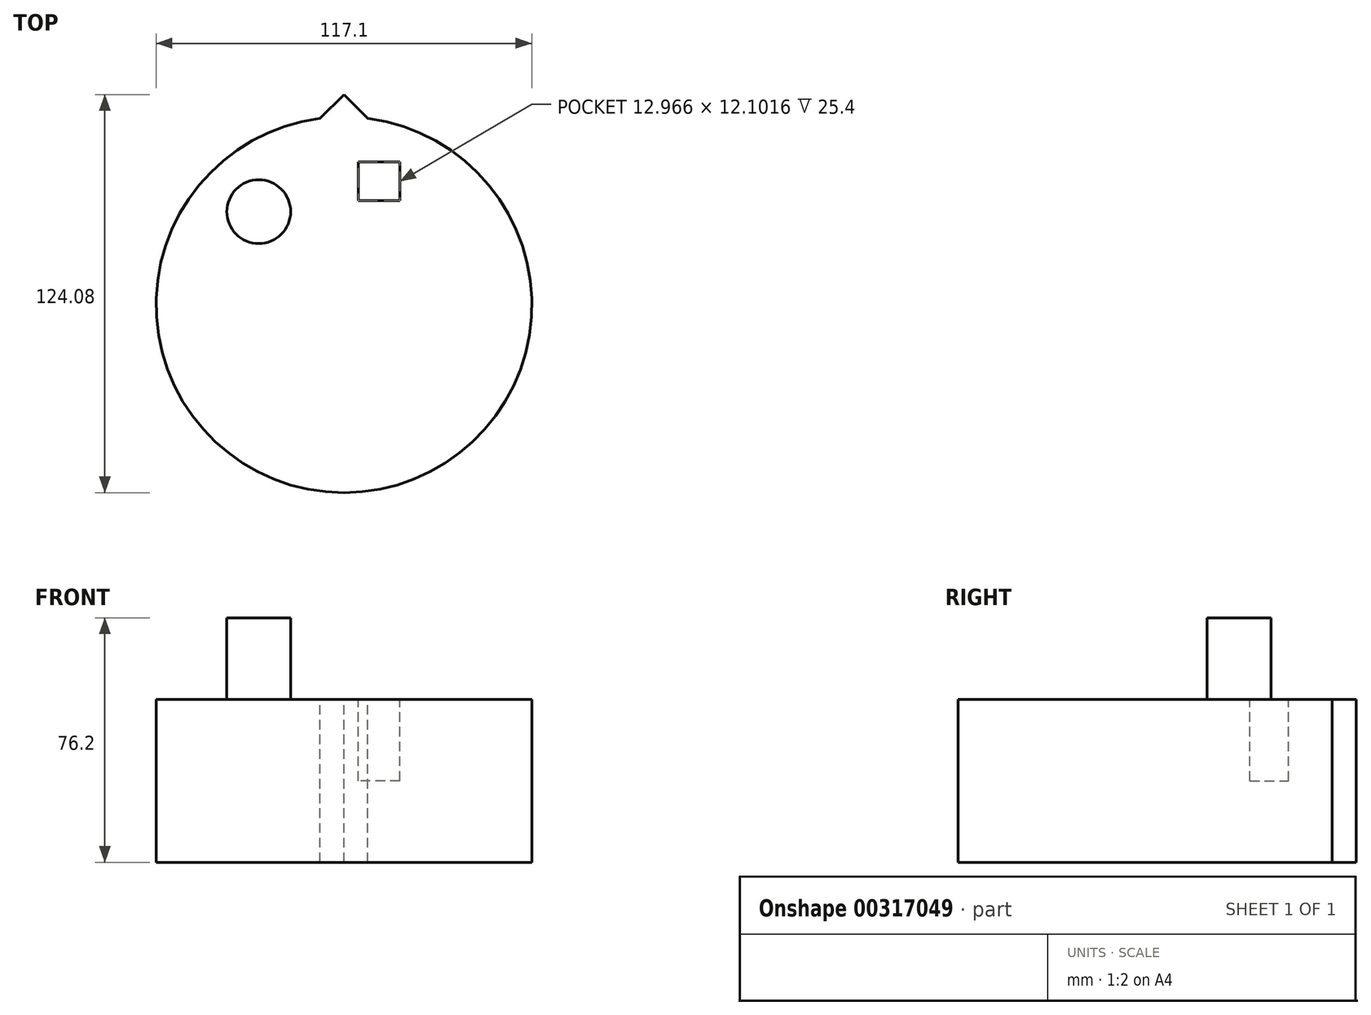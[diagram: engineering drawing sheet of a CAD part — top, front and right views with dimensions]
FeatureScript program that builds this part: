
annotation { "Feature Type Name" : "Feature", "Feature Type Description" : "" }
export const myFeature = defineFeature(function(context is Context, id is Id, definition is map)
    precondition{}
    {
        {
            var Q0;
            Q0=qCreatedBy(makeId("Top.planeOp"),FACE);
            var sketch = newSketch(context, id + "F0", { "sketchPlane" : qUnion([Q0])});
            skCircle(sketch, "E0", {"center": v(0, 0) * mm, "radius": 58.55 * mm});
            skSolve(sketch);
        }
        {
            var Q0;
            Q0 = qSketchRegion(id + "F0", true);
            extrude(context, id + "F1", {"entities" : qUnion([Q0]), "depth" : 50.8 * mm, "symmetric" : true});
        }
        {
            var Q0;
            Q0=makeQuery(id+"F1.opExtrude","CAP_FACE",FACE,{"disambiguationData":[OSD([sQuery(id+"F0.wireOp",EDGE,"E0")])],"isStart":false});
            var sketch = newSketch(context, id + "F2", { "sketchPlane" : qUnion([Q0])});
            skCircle(sketch, "E1", {"center": v(-26.56, 29) * mm, "radius": 9.94 * mm});
            skSolve(sketch);
        }
        {
            var Q0;
            Q0 = qSketchRegion(id + "F2", true);
            extrude(context, id + "F3", {"entities" : qUnion([Q0]), "operationType" : NewBodyOperationType.ADD, "depth" : 25.4 * mm});
        }
        {
            var Q0;
            Q0=makeQuery(id+"F1.opExtrude","CAP_FACE",FACE,{"disambiguationData":[OSD([sQuery(id+"F0.wireOp",EDGE,"E0")])],"isStart":false});
            var sketch = newSketch(context, id + "F4", { "sketchPlane" : qUnion([Q0])});
            skLineSegment(sketch, "E2", {"start": v(-7.45, 58.08) * mm, "end": v(0, 65.53) * mm});
            skLineSegment(sketch, "E3", {"start": v(0, 65.53) * mm, "end": v(7.45, 58.08) * mm});
            skSolve(sketch);
        }
        {
            var Q0;
            Q0 = qSketchRegion(id + "F4", true);
            var Q1;
            {var subQ0=sQuery(id+"F4.wireOp",EDGE,"E2");Q1=makeQuery(id+"F4.imprint","IMPRINT",FACE,{"disambiguationData":[TD([[makeQuery(id+"F4.imprint","IMPRINT",EDGE,{"derivedFrom":subQ0}),-1.0]])]});}
            var Q2;
            Q2=makeQuery(id+"F1.opExtrude","CAP_FACE",FACE,{"disambiguationData":[OSD([sQuery(id+"F0.wireOp",EDGE,"E0")])],"isStart":true});
            extrude(context, id + "F5", {"entities" : qUnion([Q0, Q1]), "operationType" : NewBodyOperationType.ADD, "endBound" : BoundingType.UP_TO_SURFACE, "oppositeDirection" : true, "endBoundEntityFace" : qUnion([Q2]), "depth" : 25.4 * mm});
        }
        {
            var Q0;
            {var subQ0=sQuery(id+"F4.wireOp",EDGE,"E3");var subQ1=sQuery(id+"F4.wireOp",EDGE,"E2");var subQ2=sQuery(id+"F0.wireOp",EDGE,"E0");Q0=makeQuery(id+"FUyhHjrvl3hoZVZ_1.7.F5.boolean.opBoolean","MERGE",FACE,{"derivedFrom":[makeQuery(id+"FUyhHjrvl3hoZVZ_1.6.F5.boolean.opBoolean","MERGE",FACE,{"derivedFrom":[makeQuery(id+"FUyhHjrvl3hoZVZ_1.5.F5.boolean.opBoolean","MERGE",FACE,{"derivedFrom":[makeQuery(id+"FUyhHjrvl3hoZVZ_1.4.F5.boolean.opBoolean","MERGE",FACE,{"derivedFrom":[makeQuery(id+"FUyhHjrvl3hoZVZ_1.3.F5.boolean.opBoolean","MERGE",FACE,{"derivedFrom":[makeQuery(id+"FUyhHjrvl3hoZVZ_1.2.F5.boolean.opBoolean","MERGE",FACE,{"derivedFrom":[makeQuery(id+"FUyhHjrvl3hoZVZ_1.1.F5.boolean.opBoolean","MERGE",FACE,{"derivedFrom":[makeQuery(id+"F5.boolean.opBoolean","MERGE",FACE,{"derivedFrom":[makeQuery(id+"F1.opExtrude","CAP_FACE",FACE,{"disambiguationData":[OSD([subQ2])],"isStart":false}),makeQuery(id+"F5.opExtrude","CAP_FACE",FACE,{"disambiguationData":[OSD([subQ2,subQ1,subQ0])],"isStart":true})]}),makeQuery(id+"FUyhHjrvl3hoZVZ_1.1.F5.opExtrude","CAP_FACE",FACE,{"disambiguationData":[OSD([subQ2,subQ1,subQ0])],"isStart":true})]}),makeQuery(id+"FUyhHjrvl3hoZVZ_1.2.F5.opExtrude","CAP_FACE",FACE,{"disambiguationData":[OSD([subQ2,subQ1,subQ0])],"isStart":true})]}),makeQuery(id+"FUyhHjrvl3hoZVZ_1.3.F5.opExtrude","CAP_FACE",FACE,{"disambiguationData":[OSD([subQ2,subQ1,subQ0])],"isStart":true})]}),makeQuery(id+"FUyhHjrvl3hoZVZ_1.4.F5.opExtrude","CAP_FACE",FACE,{"disambiguationData":[OSD([subQ2,subQ1,subQ0])],"isStart":true})]}),makeQuery(id+"FUyhHjrvl3hoZVZ_1.5.F5.opExtrude","CAP_FACE",FACE,{"disambiguationData":[OSD([subQ2,subQ1,subQ0])],"isStart":true})]}),makeQuery(id+"FUyhHjrvl3hoZVZ_1.6.F5.opExtrude","CAP_FACE",FACE,{"disambiguationData":[OSD([subQ2,subQ1,subQ0])],"isStart":true})]}),makeQuery(id+"FUyhHjrvl3hoZVZ_1.7.F5.opExtrude","CAP_FACE",FACE,{"disambiguationData":[OSD([subQ2,subQ1,subQ0])],"isStart":true})]});}
            var sketch = newSketch(context, id + "F6", { "sketchPlane" : qUnion([Q0])});
            skLineSegment(sketch, "E4.bottom", {"start": v(17.39, 32.4) * mm, "end": v(4.42, 32.4) * mm});
            skLineSegment(sketch, "E4.top", {"start": v(17.39, 44.5) * mm, "end": v(4.42, 44.5) * mm});
            skLineSegment(sketch, "E4.left", {"start": v(17.39, 32.4) * mm, "end": v(17.39, 44.5) * mm});
            skLineSegment(sketch, "E4.right", {"start": v(4.42, 32.4) * mm, "end": v(4.42, 44.5) * mm});
            skPoint(sketch, "E4.middle", {"position": v(10.9, 38.44) * mm});
            skSolve(sketch);
        }
        {
            var Q0;
            Q0 = qSketchRegion(id + "F6", true);
            extrude(context, id + "F7", {"entities" : qUnion([Q0]), "operationType" : NewBodyOperationType.REMOVE, "oppositeDirection" : true, "depth" : 25.4 * mm});
        }
    });
